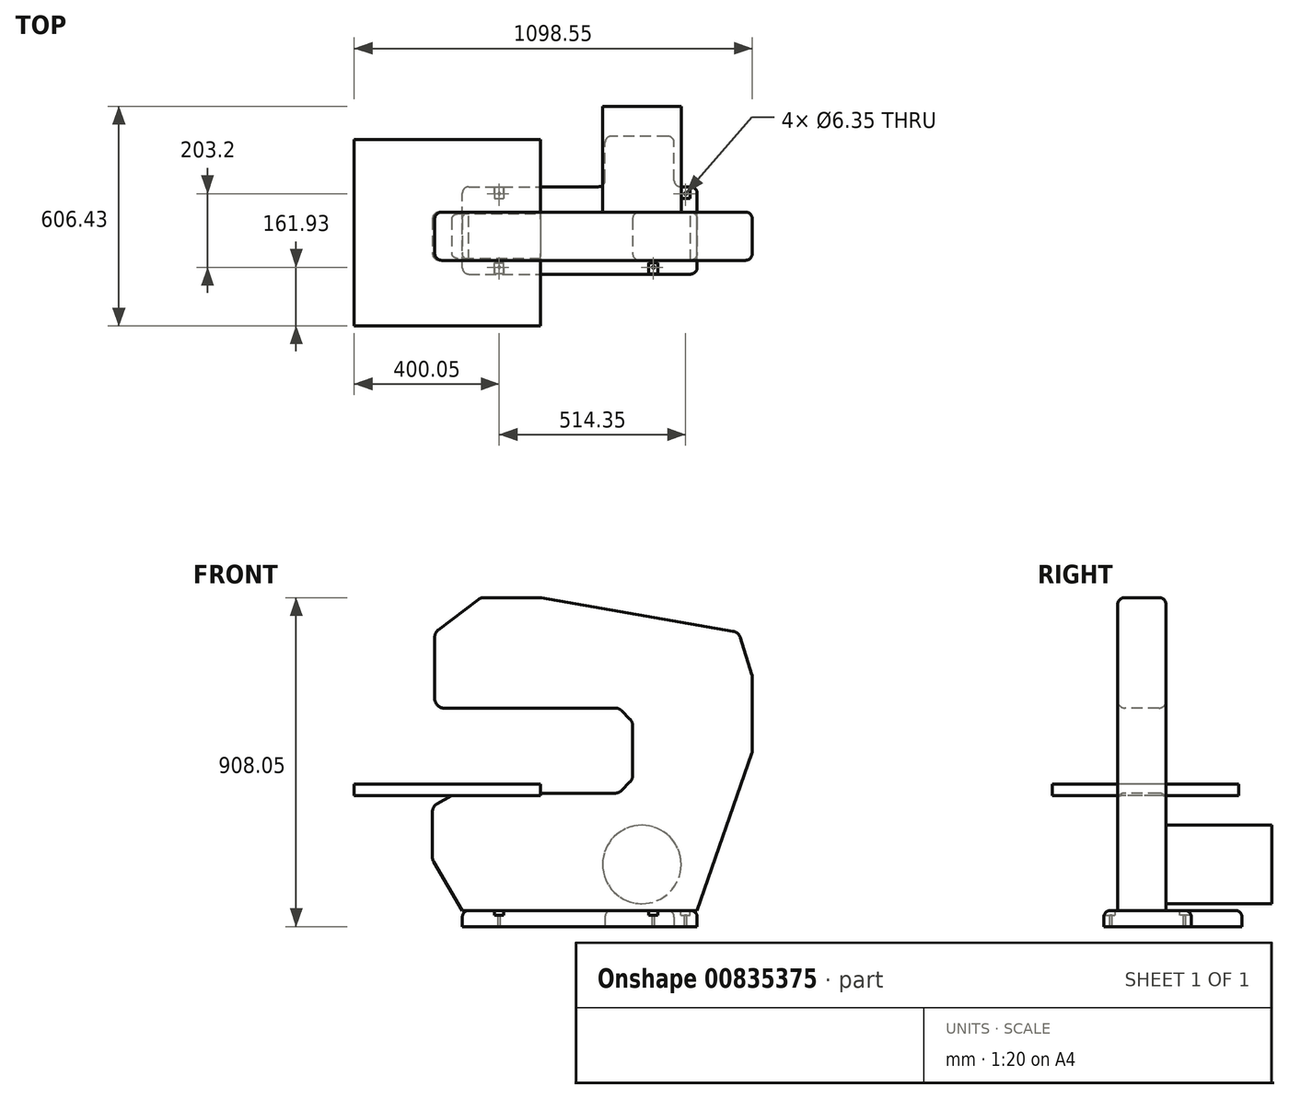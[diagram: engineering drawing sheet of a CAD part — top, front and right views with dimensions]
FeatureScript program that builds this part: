
annotation { "Feature Type Name" : "Feature", "Feature Type Description" : "" }
export const myFeature = defineFeature(function(context is Context, id is Id, definition is map)
    precondition{}
    {
        {
            var Q0;
            Q0=qCreatedBy(makeId("Top.planeOp"),FACE);
            var sketch = newSketch(context, id + "F0", { "sketchPlane" : qUnion([Q0])});
            skLineSegment(sketch, "E0.bottom", {"start": v(0, 0) * mm, "end": v(647.7, 0) * mm});
            skLineSegment(sketch, "E0.top", {"start": v(0, 241.3) * mm, "end": v(393.7, 241.3) * mm});
            skLineSegment(sketch, "E0.left", {"start": v(0, 0) * mm, "end": v(0, 241.3) * mm});
            skLineSegment(sketch, "E0.right", {"start": v(647.7, 0) * mm, "end": v(647.7, 241.3) * mm});
            skLineSegment(sketch, "E1.top", {"start": v(584.2, 381) * mm, "end": v(393.7, 381) * mm});
            skLineSegment(sketch, "E1.left", {"start": v(584.2, 241.3) * mm, "end": v(584.2, 381) * mm});
            skLineSegment(sketch, "E1.right", {"start": v(393.7, 241.3) * mm, "end": v(393.7, 381) * mm});
            skLineSegment(sketch, "E2.trimOffspring", {"start": v(584.2, 241.3) * mm, "end": v(647.7, 241.3) * mm});
            skSolve(sketch);
        }
        {
            var Q0;
            Q0 = qSketchRegion(id + "F0", true);
            extrude(context, id + "F1", {"entities" : qUnion([Q0]), "depth" : 44.45 * mm, "offsetDistance" : 25.4 * mm});
        }
        {
            var Q0;
            Q0=makeQuery(id+"F1.opExtrude","SWEPT_EDGE",EDGE,{"disambiguationData":[OSD([sQuery(id+"F0.wireOp",EDGE,"E0.bottom"),sQuery(id+"F0.wireOp",EDGE,"E0.right")])]});
            var Q1;
            Q1=makeQuery(id+"F1.opExtrude","SWEPT_EDGE",EDGE,{"disambiguationData":[OSD([sQuery(id+"F0.wireOp",EDGE,"E0.right"),sQuery(id+"F0.wireOp",EDGE,"E2.trimOffspring")])]});
            var Q2;
            Q2=makeQuery(id+"F1.opExtrude","SWEPT_EDGE",EDGE,{"disambiguationData":[OSD([sQuery(id+"F0.wireOp",EDGE,"E1.left"),sQuery(id+"F0.wireOp",EDGE,"E2.trimOffspring")])]});
            var Q3;
            Q3=makeQuery(id+"F1.opExtrude","SWEPT_EDGE",EDGE,{"disambiguationData":[OSD([sQuery(id+"F0.wireOp",EDGE,"E1.top"),sQuery(id+"F0.wireOp",EDGE,"E1.left")])]});
            var Q4;
            Q4=makeQuery(id+"F1.opExtrude","SWEPT_EDGE",EDGE,{"disambiguationData":[OSD([sQuery(id+"F0.wireOp",EDGE,"E1.top"),sQuery(id+"F0.wireOp",EDGE,"E1.right")])]});
            var Q5;
            Q5=makeQuery(id+"F1.opExtrude","SWEPT_EDGE",EDGE,{"disambiguationData":[OSD([sQuery(id+"F0.wireOp",EDGE,"E0.top"),sQuery(id+"F0.wireOp",EDGE,"E1.right")])]});
            var Q6;
            Q6=makeQuery(id+"F1.opExtrude","SWEPT_EDGE",EDGE,{"disambiguationData":[OSD([sQuery(id+"F0.wireOp",EDGE,"E0.top"),sQuery(id+"F0.wireOp",EDGE,"E0.left")])]});
            var Q7;
            Q7=makeQuery(id+"F1.opExtrude","SWEPT_EDGE",EDGE,{"disambiguationData":[OSD([sQuery(id+"F0.wireOp",EDGE,"E0.bottom"),sQuery(id+"F0.wireOp",EDGE,"E0.left")])]});
            fillet(context, id + "F2", {"entities" : qUnion([Q0, Q1, Q2, Q3, Q4, Q5, Q6, Q7]), "radius" : 17.78 * mm, "tangentPropagation" : true, "allowEdgeOverflow" : false});
        }
        {
            var Q0;
            Q0=makeQuery(id+"F1.opExtrude","CAP_EDGE",EDGE,{"disambiguationData":[OSD([sQuery(id+"F0.wireOp",EDGE,"E0.bottom")])],"isStart":false});
            fillet(context, id + "F3", {"entities" : qUnion([Q0]), "radius" : 17.78 * mm, "tangentPropagation" : true, "allowEdgeOverflow" : false});
        }
        {
            var Q0;
            Q0=makeQuery(id+"F1.opExtrude","CAP_FACE",FACE,{"disambiguationData":[OSD([sQuery(id+"F0.wireOp",EDGE,"E0.bottom"),sQuery(id+"F0.wireOp",EDGE,"E0.top"),sQuery(id+"F0.wireOp",EDGE,"E0.left"),sQuery(id+"F0.wireOp",EDGE,"E0.right"),sQuery(id+"F0.wireOp",EDGE,"E1.top"),sQuery(id+"F0.wireOp",EDGE,"E1.left"),sQuery(id+"F0.wireOp",EDGE,"E1.right"),sQuery(id+"F0.wireOp",EDGE,"E2.trimOffspring")])],"isStart":false});
            var sketch = newSketch(context, id + "F4", { "sketchPlane" : qUnion([Q0])});
            skLineSegment(sketch, "E3.bottom", {"start": v(88.9, 0) * mm, "end": v(114.3, 0) * mm});
            skLineSegment(sketch, "E3.top", {"start": v(88.9, 31.75) * mm, "end": v(114.3, 31.75) * mm});
            skLineSegment(sketch, "E3.left", {"start": v(88.9, 0) * mm, "end": v(88.9, 31.75) * mm});
            skLineSegment(sketch, "E3.right", {"start": v(114.3, 0) * mm, "end": v(114.3, 31.75) * mm});
            skLineSegment(sketch, "E4.bottom", {"start": v(514.35, 0) * mm, "end": v(539.75, 0) * mm});
            skLineSegment(sketch, "E4.top", {"start": v(514.35, 31.75) * mm, "end": v(539.75, 31.75) * mm});
            skLineSegment(sketch, "E4.left", {"start": v(514.35, 0) * mm, "end": v(514.35, 31.75) * mm});
            skLineSegment(sketch, "E4.right", {"start": v(539.75, 0) * mm, "end": v(539.75, 31.75) * mm});
            skLineSegment(sketch, "E5.bottom", {"start": v(628.65, 209.55) * mm, "end": v(603.25, 209.55) * mm});
            skLineSegment(sketch, "E5.top", {"start": v(628.65, 241.3) * mm, "end": v(603.25, 241.3) * mm});
            skLineSegment(sketch, "E5.left", {"start": v(628.65, 209.55) * mm, "end": v(628.65, 241.3) * mm});
            skLineSegment(sketch, "E5.right", {"start": v(603.25, 209.55) * mm, "end": v(603.25, 241.3) * mm});
            skLineSegment(sketch, "E6.bottom", {"start": v(88.9, 241.3) * mm, "end": v(114.3, 241.3) * mm});
            skLineSegment(sketch, "E6.top", {"start": v(88.9, 209.55) * mm, "end": v(114.3, 209.55) * mm});
            skLineSegment(sketch, "E6.left", {"start": v(88.9, 241.3) * mm, "end": v(88.9, 209.55) * mm});
            skLineSegment(sketch, "E6.right", {"start": v(114.3, 241.3) * mm, "end": v(114.3, 209.55) * mm});
            skLineSegment(sketch, "E7", {"start": v(527.05, 0) * mm, "end": v(527.05, 31.75) * mm, "construction": true});
            skLineSegment(sketch, "E8", {"start": v(101.6, 0) * mm, "end": v(101.6, 31.75) * mm, "construction": true});
            skLineSegment(sketch, "E9", {"start": v(101.6, 209.55) * mm, "end": v(101.6, 241.3) * mm, "construction": true});
            skLineSegment(sketch, "E10", {"start": v(615.95, 209.55) * mm, "end": v(615.95, 241.3) * mm, "construction": true});
            skSolve(sketch);
        }
        {
            var Q0;
            Q0 = qSketchRegion(id + "F4", true);
            extrude(context, id + "F5", {"entities" : qUnion([Q0]), "operationType" : NewBodyOperationType.REMOVE, "oppositeDirection" : true, "depth" : 12.7 * mm, "offsetDistance" : 25.4 * mm});
        }
        {
            var Q0;
            Q0=makeQuery(id+"F5.boolean.opBoolean","COPY",FACE,{"derivedFrom":makeQuery(id+"F5.opExtrude","CAP_FACE",FACE,{"disambiguationData":[OSD([sQuery(id+"F4.wireOp",EDGE,"E4.bottom"),sQuery(id+"F4.wireOp",EDGE,"E4.top"),sQuery(id+"F4.wireOp",EDGE,"E4.left"),sQuery(id+"F4.wireOp",EDGE,"E4.right")])],"isStart":false})});
            var sketch = newSketch(context, id + "F6", { "sketchPlane" : qUnion([Q0])});
            skCircle(sketch, "E11", {"center": v(527.05, 19.05) * mm, "radius": 3.18 * mm});
            skCircle(sketch, "E12", {"center": v(101.6, 19.05) * mm, "radius": 3.18 * mm});
            skCircle(sketch, "E13", {"center": v(101.6, 222.25) * mm, "radius": 3.18 * mm});
            skCircle(sketch, "E14", {"center": v(615.95, 222.25) * mm, "radius": 3.18 * mm});
            skSolve(sketch);
        }
        {
            var Q0;
            Q0 = qSketchRegion(id + "F6", true);
            extrude(context, id + "F7", {"entities" : qUnion([Q0]), "operationType" : NewBodyOperationType.REMOVE, "endBound" : BoundingType.THROUGH_ALL, "oppositeDirection" : true, "depth" : 25.4 * mm, "offsetDistance" : 25.4 * mm});
        }
        {
            var Q0;
            Q0=qCreatedBy(makeId("Front.planeOp"),FACE);
            cPlane(context, id + "F8", {"entities" : qUnion([Q0]), "cplaneType" : CPlaneType.OFFSET, "offset" : 38.1 * mm, "oppositeDirection" : true, "width" : 152.4 * mm, "height" : 152.4 * mm});
        }
        {
            var Q0;
            Q0=qCreatedBy(id+"F8.planeOp",FACE);
            var sketch = newSketch(context, id + "F9", { "sketchPlane" : qUnion([Q0])});
            skLineSegment(sketch, "E15", {"start": v(0, 44.45) * mm, "end": v(647.7, 44.45) * mm});
            skLineSegment(sketch, "E16", {"start": v(647.7, 44.45) * mm, "end": v(800.1, 482.6) * mm});
            skLineSegment(sketch, "E17", {"start": v(0, 44.45) * mm, "end": v(-82.55, 184.15) * mm});
            skLineSegment(sketch, "E18", {"start": v(800.1, 482.6) * mm, "end": v(800.1, 692.15) * mm});
            skLineSegment(sketch, "E19", {"start": v(800.1, 692.15) * mm, "end": v(762, 812.8) * mm});
            skLineSegment(sketch, "E20", {"start": v(762, 812.8) * mm, "end": v(215.9, 908.05) * mm});
            skLineSegment(sketch, "E21", {"start": v(215.9, 908.05) * mm, "end": v(50.8, 908.05) * mm});
            skLineSegment(sketch, "E22", {"start": v(50.8, 908.05) * mm, "end": v(-76.2, 811.4) * mm});
            skLineSegment(sketch, "E23", {"start": v(-76.2, 811.4) * mm, "end": v(-76.2, 603.25) * mm});
            skLineSegment(sketch, "E24", {"start": v(-76.2, 603.25) * mm, "end": v(431.8, 603.25) * mm});
            skLineSegment(sketch, "E25", {"start": v(469.9, 565.15) * mm, "end": v(469.9, 406.4) * mm});
            skLineSegment(sketch, "E26", {"start": v(431.8, 368.3) * mm, "end": v(-18.66, 368.3) * mm});
            skLineSegment(sketch, "E27", {"start": v(-82.55, 184.15) * mm, "end": v(-82.55, 331.33) * mm});
            skLineSegment(sketch, "E28", {"start": v(-82.55, 331.33) * mm, "end": v(-18.66, 368.3) * mm});
            skLineSegment(sketch, "E29", {"start": v(431.8, 368.3) * mm, "end": v(469.9, 406.4) * mm});
            skLineSegment(sketch, "E30", {"start": v(431.8, 603.25) * mm, "end": v(469.9, 565.15) * mm});
            skPoint(sketch, "E31.orphan", {"position": v(469.9, 603.25) * mm});
            skPoint(sketch, "E32.orphan", {"position": v(469.9, 368.3) * mm});
            skSolve(sketch);
        }
        {
            var Q0;
            Q0 = qSketchRegion(id + "F9", true);
            extrude(context, id + "F10", {"entities" : qUnion([Q0]), "operationType" : NewBodyOperationType.ADD, "oppositeDirection" : true, "depth" : 133.35 * mm, "offsetDistance" : 25.4 * mm});
        }
        {
            var Q0;
            Q0=makeQuery(id+"F10.opExtrude","SWEPT_EDGE",EDGE,{"disambiguationData":[OSD([sQuery(id+"F9.wireOp",EDGE,"E17"),sQuery(id+"F9.wireOp",EDGE,"E27")])]});
            var Q1;
            Q1=makeQuery(id+"F10.opExtrude","SWEPT_EDGE",EDGE,{"disambiguationData":[OSD([sQuery(id+"F9.wireOp",EDGE,"E27"),sQuery(id+"F9.wireOp",EDGE,"E28")])]});
            var Q2;
            Q2=makeQuery(id+"F10.opExtrude","SWEPT_EDGE",EDGE,{"disambiguationData":[OSD([sQuery(id+"F9.wireOp",EDGE,"E26"),sQuery(id+"F9.wireOp",EDGE,"E28")])]});
            var Q3;
            Q3=makeQuery(id+"F10.opExtrude","SWEPT_EDGE",EDGE,{"disambiguationData":[OSD([sQuery(id+"F9.wireOp",EDGE,"E26"),sQuery(id+"F9.wireOp",EDGE,"E29")])]});
            var Q4;
            Q4=makeQuery(id+"F10.opExtrude","SWEPT_EDGE",EDGE,{"disambiguationData":[OSD([sQuery(id+"F9.wireOp",EDGE,"E25"),sQuery(id+"F9.wireOp",EDGE,"E29")])]});
            var Q5;
            Q5=makeQuery(id+"F10.opExtrude","SWEPT_EDGE",EDGE,{"disambiguationData":[OSD([sQuery(id+"F9.wireOp",EDGE,"E25"),sQuery(id+"F9.wireOp",EDGE,"E30")])]});
            var Q6;
            Q6=makeQuery(id+"F10.opExtrude","SWEPT_EDGE",EDGE,{"disambiguationData":[OSD([sQuery(id+"F9.wireOp",EDGE,"E24"),sQuery(id+"F9.wireOp",EDGE,"E30")])]});
            var Q7;
            Q7=makeQuery(id+"F10.opExtrude","SWEPT_EDGE",EDGE,{"disambiguationData":[OSD([sQuery(id+"F9.wireOp",EDGE,"E23"),sQuery(id+"F9.wireOp",EDGE,"E24")])]});
            var Q8;
            Q8=makeQuery(id+"F10.opExtrude","SWEPT_EDGE",EDGE,{"disambiguationData":[OSD([sQuery(id+"F9.wireOp",EDGE,"E22"),sQuery(id+"F9.wireOp",EDGE,"E23")])]});
            var Q9;
            Q9=makeQuery(id+"F10.opExtrude","SWEPT_EDGE",EDGE,{"disambiguationData":[OSD([sQuery(id+"F9.wireOp",EDGE,"E21"),sQuery(id+"F9.wireOp",EDGE,"E22")])]});
            var Q10;
            Q10=makeQuery(id+"F10.opExtrude","SWEPT_EDGE",EDGE,{"disambiguationData":[OSD([sQuery(id+"F9.wireOp",EDGE,"E20"),sQuery(id+"F9.wireOp",EDGE,"E21")])]});
            var Q11;
            Q11=makeQuery(id+"F10.opExtrude","SWEPT_EDGE",EDGE,{"disambiguationData":[OSD([sQuery(id+"F9.wireOp",EDGE,"E19"),sQuery(id+"F9.wireOp",EDGE,"E20")])]});
            var Q12;
            Q12=makeQuery(id+"F10.opExtrude","SWEPT_EDGE",EDGE,{"disambiguationData":[OSD([sQuery(id+"F9.wireOp",EDGE,"E18"),sQuery(id+"F9.wireOp",EDGE,"E19")])]});
            var Q13;
            Q13=makeQuery(id+"F10.opExtrude","SWEPT_EDGE",EDGE,{"disambiguationData":[OSD([sQuery(id+"F9.wireOp",EDGE,"E16"),sQuery(id+"F9.wireOp",EDGE,"E18")])]});
            fillet(context, id + "F11", {"entities" : qUnion([Q0, Q1, Q2, Q3, Q4, Q5, Q6, Q7, Q8, Q9, Q10, Q11, Q12, Q13]), "radius" : 25.4 * mm, "tangentPropagation" : true, "allowEdgeOverflow" : false});
        }
        {
            var Q0;
            Q0=makeQuery(id+"F10.opExtrude","CAP_EDGE",EDGE,{"disambiguationData":[OSD([sQuery(id+"F9.wireOp",EDGE,"E16")])],"isStart":true});
            var Q1;
            Q1=makeQuery(id+"F10.opExtrude","CAP_EDGE",EDGE,{"disambiguationData":[OSD([sQuery(id+"F9.wireOp",EDGE,"E16")])],"isStart":false});
            fillet(context, id + "F12", {"entities" : qUnion([Q0, Q1]), "radius" : 19.05 * mm, "tangentPropagation" : true, "allowEdgeOverflow" : false});
        }
        {
            var Q0;
            Q0=qCreatedBy(makeId("Top.planeOp"),FACE);
            cPlane(context, id + "F13", {"entities" : qUnion([Q0]), "cplaneType" : CPlaneType.OFFSET, "offset" : 393.7 * mm, "width" : 152.4 * mm, "height" : 152.4 * mm});
        }
        {
            var Q0;
            Q0=qCreatedBy(id+"F13.planeOp",FACE);
            var sketch = newSketch(context, id + "F14", { "sketchPlane" : qUnion([Q0])});
            skLineSegment(sketch, "E33.bottom", {"start": v(-298.45, 371.48) * mm, "end": v(215.9, 371.48) * mm});
            skLineSegment(sketch, "E33.top", {"start": v(-298.45, -142.88) * mm, "end": v(215.9, -142.88) * mm});
            skLineSegment(sketch, "E33.left", {"start": v(-298.45, 371.48) * mm, "end": v(-298.45, -142.88) * mm});
            skLineSegment(sketch, "E33.right", {"start": v(215.9, 371.48) * mm, "end": v(215.9, -142.88) * mm});
            skSolve(sketch);
        }
        {
            var Q0;
            Q0 = qSketchRegion(id + "F14", true);
            extrude(context, id + "F15", {"entities" : qUnion([Q0]), "operationType" : NewBodyOperationType.ADD, "oppositeDirection" : true, "depth" : 31.75 * mm, "offsetDistance" : 25.4 * mm});
        }
        {
            var Q0;
            Q0=makeQuery(id+"F10.opExtrude","CAP_FACE",FACE,{"disambiguationData":[OSD([sQuery(id+"F9.wireOp",EDGE,"E15"),sQuery(id+"F9.wireOp",EDGE,"E16"),sQuery(id+"F9.wireOp",EDGE,"E17"),sQuery(id+"F9.wireOp",EDGE,"E18"),sQuery(id+"F9.wireOp",EDGE,"E19"),sQuery(id+"F9.wireOp",EDGE,"E20"),sQuery(id+"F9.wireOp",EDGE,"E21"),sQuery(id+"F9.wireOp",EDGE,"E22"),sQuery(id+"F9.wireOp",EDGE,"E23"),sQuery(id+"F9.wireOp",EDGE,"E24"),sQuery(id+"F9.wireOp",EDGE,"E25"),sQuery(id+"F9.wireOp",EDGE,"E26"),sQuery(id+"F9.wireOp",EDGE,"E27"),sQuery(id+"F9.wireOp",EDGE,"E28"),sQuery(id+"F9.wireOp",EDGE,"E29"),sQuery(id+"F9.wireOp",EDGE,"E30")])],"isStart":false});
            var sketch = newSketch(context, id + "F16", { "sketchPlane" : qUnion([Q0])});
            skCircle(sketch, "E34", {"center": v(-495.3, 171.45) * mm, "radius": 108.35 * mm});
            skSolve(sketch);
        }
        {
            var Q0;
            Q0 = qSketchRegion(id + "F16", true);
            extrude(context, id + "F17", {"entities" : qUnion([Q0]), "operationType" : NewBodyOperationType.ADD, "depth" : 292.1 * mm, "offsetDistance" : 25.4 * mm});
        }
    });
